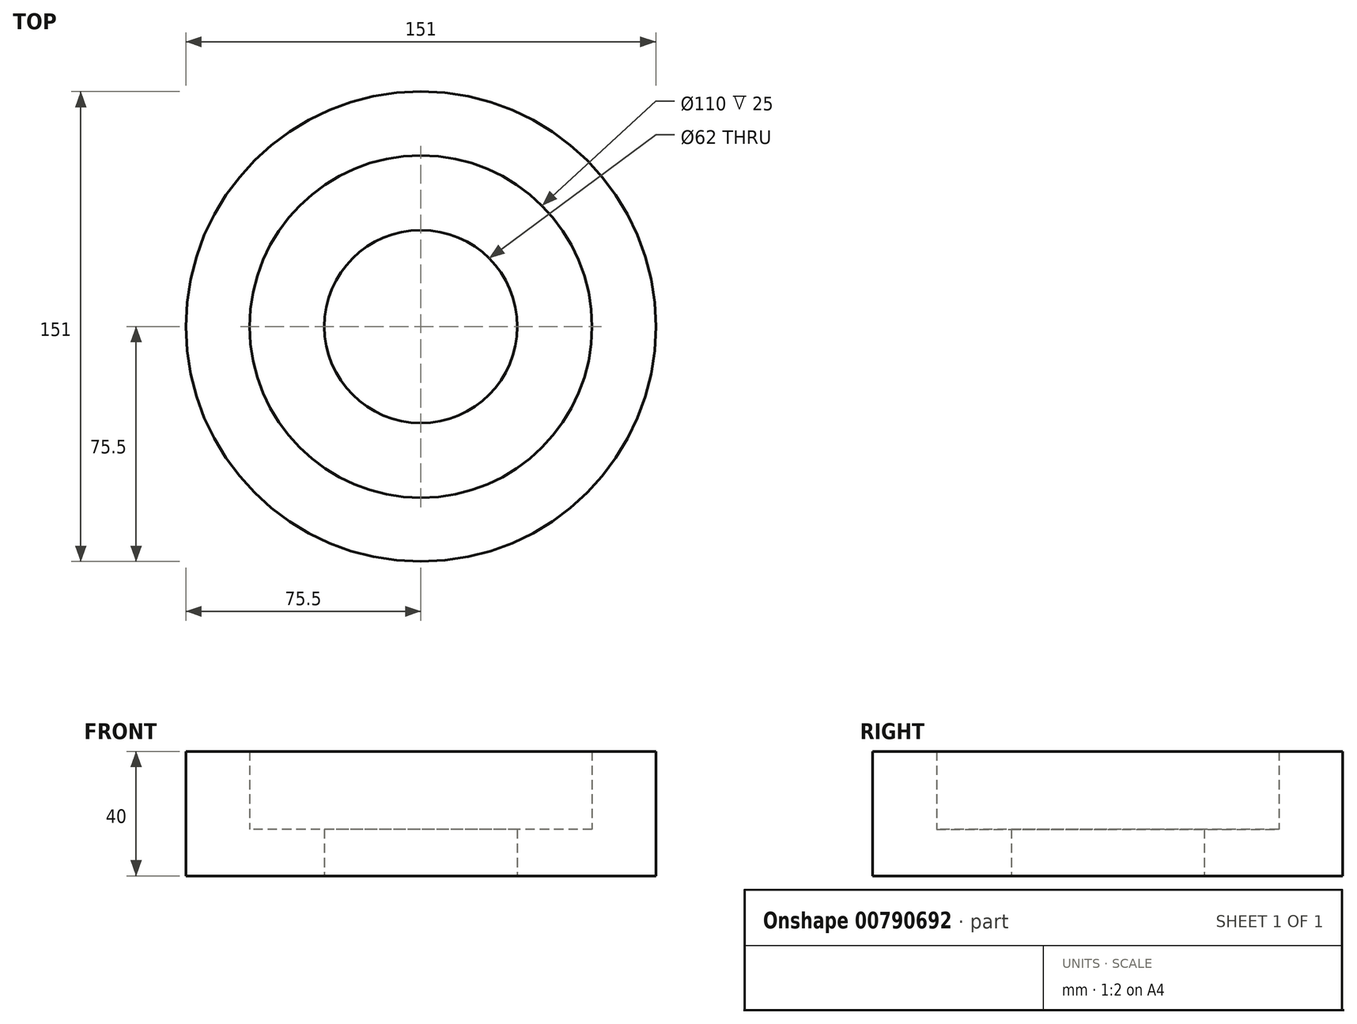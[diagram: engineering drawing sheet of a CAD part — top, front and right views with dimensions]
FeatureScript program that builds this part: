
annotation { "Feature Type Name" : "Feature", "Feature Type Description" : "" }
export const myFeature = defineFeature(function(context is Context, id is Id, definition is map)
    precondition{}
    {
        {
            var Q0;
            Q0=qCreatedBy(makeId("Top.planeOp"),FACE);
            var sketch = newSketch(context, id + "F0", { "sketchPlane" : qUnion([Q0])});
            skCircle(sketch, "E0", {"center": v(0, 0) * mm, "radius": 31 * mm});
            skCircle(sketch, "E1", {"center": v(0, 0) * mm, "radius": 75.5 * mm});
            skCircle(sketch, "E2", {"center": v(0, 0) * mm, "radius": 55 * mm});
            skSolve(sketch);
        }
        {
            var Q0;
            Q0=makeQuery(id+"F0.imprint","IMPRINT",FACE,{"disambiguationData":[TD([[makeQuery(id+"F0.imprint","IMPRINT",EDGE,{"derivedFrom":sQuery(id+"F0.wireOp",EDGE,"E1")}),1.0]])]});
            extrude(context, id + "F1", {"entities" : qUnion([Q0]), "depth" : (25 + 15) * mm, "offsetDistance" : 25 * mm});
        }
        {
            var Q0;
            Q0=makeQuery(id+"F0.imprint","IMPRINT",FACE,{"disambiguationData":[TD([[makeQuery(id+"F0.imprint","IMPRINT",EDGE,{"derivedFrom":sQuery(id+"F0.wireOp",EDGE,"E0")}),-1.0]])]});
            extrude(context, id + "F2", {"entities" : qUnion([Q0]), "operationType" : NewBodyOperationType.ADD, "depth" : 15 * mm, "offsetDistance" : 25 * mm});
        }
    });
